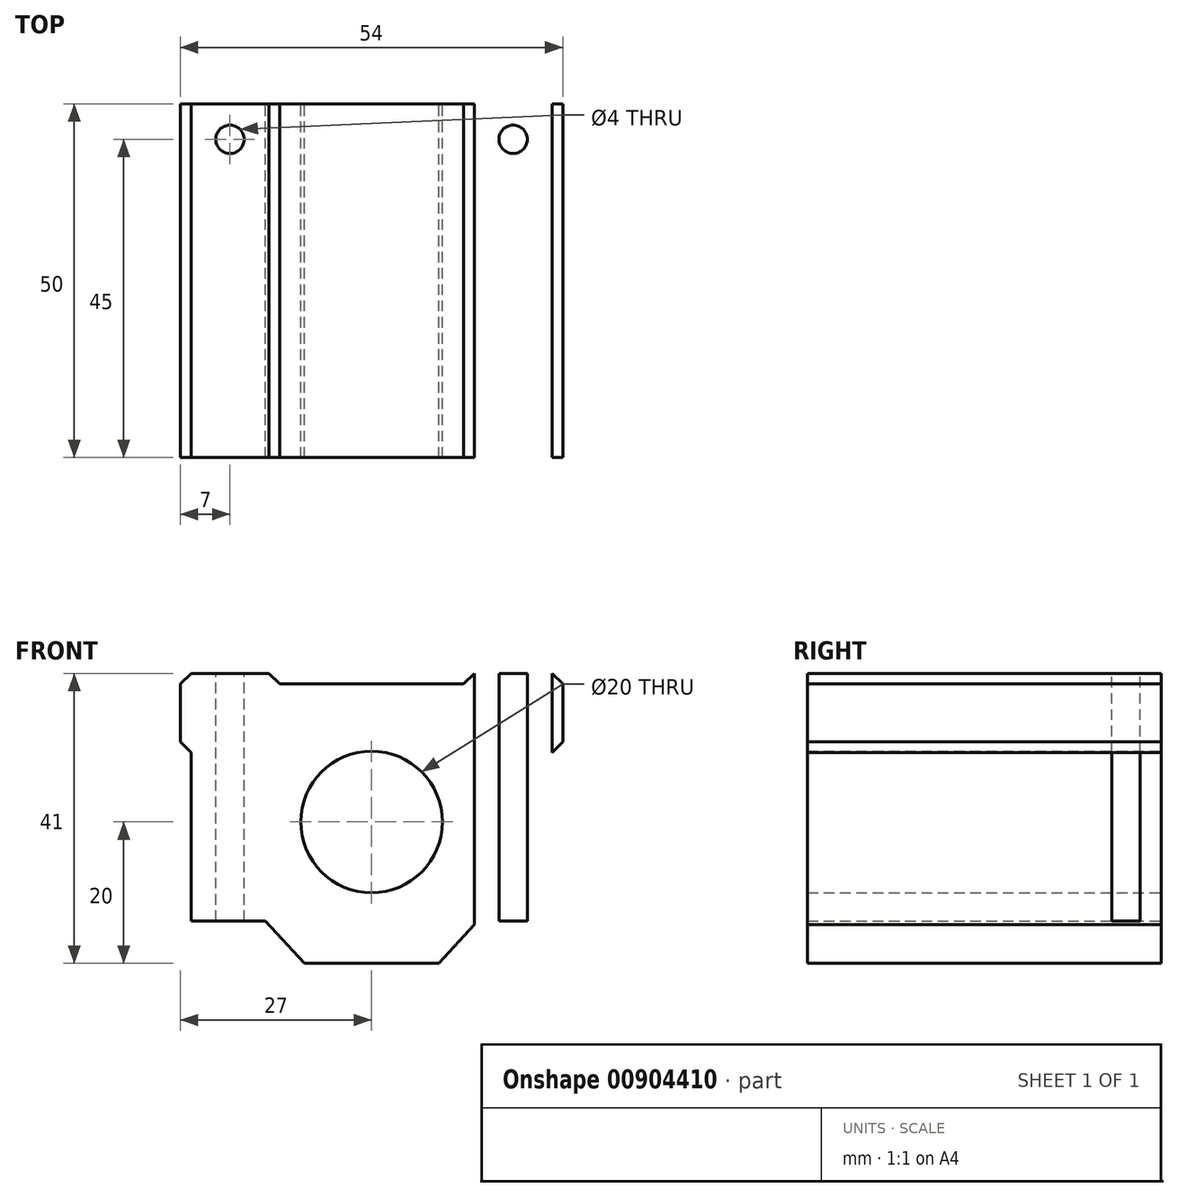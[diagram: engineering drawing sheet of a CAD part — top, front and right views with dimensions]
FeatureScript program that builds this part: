
annotation { "Feature Type Name" : "Feature", "Feature Type Description" : "" }
export const myFeature = defineFeature(function(context is Context, id is Id, definition is map)
    precondition{}
    {
        {
            var Q0;
            Q0=qCreatedBy(makeId("Front.planeOp"),FACE);
            var sketch = newSketch(context, id + "F0", { "sketchPlane" : qUnion([Q0])});
            skLineSegment(sketch, "E0", {"start": v(-9.5, -20) * mm, "end": v(-15, -14) * mm});
            skLineSegment(sketch, "E1", {"start": v(-15, -14) * mm, "end": v(-25.5, -14) * mm});
            skLineSegment(sketch, "E2", {"start": v(-25.5, -14) * mm, "end": v(-25.5, 9.82) * mm});
            skLineSegment(sketch, "E3", {"start": v(-25.5, 9.82) * mm, "end": v(-27, 11.32) * mm});
            skLineSegment(sketch, "E4", {"start": v(-27, 11.32) * mm, "end": v(-27, 19.5) * mm});
            skLineSegment(sketch, "E5", {"start": v(-27, 19.5) * mm, "end": v(-25.5, 21) * mm});
            skLineSegment(sketch, "E6", {"start": v(-25.5, 21) * mm, "end": v(-14.5, 21) * mm});
            skLineSegment(sketch, "E7", {"start": v(-14.5, 21) * mm, "end": v(-13, 19.5) * mm});
            skLineSegment(sketch, "E8.MirrorCS", {"start": v(25.5, 9.82) * mm, "end": v(27, 11.32) * mm});
            skLineSegment(sketch, "E9.MirrorCS", {"start": v(27, 19.5) * mm, "end": v(25.5, 21) * mm});
            skLineSegment(sketch, "E10.MirrorCS", {"start": v(14.5, 21) * mm, "end": v(13, 19.5) * mm});
            skLineSegment(sketch, "E11.MirrorCS", {"start": v(9.5, -20) * mm, "end": v(15, -14) * mm});
            skLineSegment(sketch, "E12.MirrorCS", {"start": v(25.5, -14) * mm, "end": v(25.5, 9.82) * mm});
            skLineSegment(sketch, "E13.MirrorCS", {"start": v(15, -14) * mm, "end": v(25.5, -14) * mm});
            skLineSegment(sketch, "E14.MirrorCS", {"start": v(27, 11.32) * mm, "end": v(27, 19.5) * mm});
            skLineSegment(sketch, "E15.MirrorCS", {"start": v(25.5, 21) * mm, "end": v(14.5, 21) * mm});
            skLineSegment(sketch, "E16", {"start": v(-13, 19.5) * mm, "end": v(13, 19.5) * mm});
            skLineSegment(sketch, "E17", {"start": v(-9.5, -20) * mm, "end": v(9.5, -20) * mm});
            skCircle(sketch, "E18", {"center": v(0, 0) * mm, "radius": 10 * mm});
            skSolve(sketch);
        }
        {
            var Q0;
            Q0=makeQuery(id+"F0.imprint","IMPRINT",FACE,{"disambiguationData":[TD([[makeQuery(id+"F0.imprint","IMPRINT",EDGE,{"derivedFrom":sQuery(id+"F0.wireOp",EDGE,"E0")}),-1.0]])]});
            extrude(context, id + "F1", {"entities" : qUnion([Q0]), "endBound" : BoundingType.SYMMETRIC, "depth" : 50 * mm, "offsetDistance" : 25 * mm});
        }
        {
            var Q0;
            Q0=makeQuery(id+"F1.opExtrude","SWEPT_FACE",FACE,{"disambiguationData":[OSD([sQuery(id+"F0.wireOp",EDGE,"E15.MirrorCS")])]});
            var sketch = newSketch(context, id + "F2", { "sketchPlane" : qUnion([Q0])});
            skLineSegment(sketch, "E19", {"start": v(28.5, 0) * mm, "end": v(-29.66, 0) * mm, "construction": true});
            skLineSegment(sketch, "E20.0", {"start": v(28.5, 20) * mm, "end": v(-29.66, 20) * mm, "construction": true});
            skLineSegment(sketch, "E21.0", {"start": v(28.5, -20) * mm, "end": v(-29.66, -20) * mm, "construction": true});
            skLineSegment(sketch, "E22", {"start": v(0, 26.59) * mm, "end": v(0, -26.5) * mm, "construction": true});
            skLineSegment(sketch, "E23.0", {"start": v(20, 26.59) * mm, "end": v(20, -26.5) * mm, "construction": true});
            skLineSegment(sketch, "E24.0", {"start": v(-20, 26.59) * mm, "end": v(-20, -26.5) * mm, "construction": true});
            skCircle(sketch, "E25", {"center": v(-20, 20) * mm, "radius": 2 * mm});
            skCircle(sketch, "E26.MirrorC", {"center": v(20, 20) * mm, "radius": 2 * mm});
            skCircle(sketch, "E27.MirrorC", {"center": v(-20, -20) * mm, "radius": 2 * mm});
            skCircle(sketch, "E28.MirrorC", {"center": v(20, -20) * mm, "radius": 2 * mm});
            skSolve(sketch);
        }
        {
            var Q0;
            Q0=makeQuery(id+"F2.imprint","IMPRINT",FACE,{"disambiguationData":[TD([[makeQuery(id+"F2.imprint","IMPRINT",EDGE,{"derivedFrom":sQuery(id+"F2.wireOp",EDGE,"E25")}),1.0]])]});
            var Q1;
            Q1=makeQuery(id+"F2.imprint","IMPRINT",FACE,{"disambiguationData":[TD([[makeQuery(id+"F2.imprint","IMPRINT",EDGE,{"derivedFrom":sQuery(id+"F2.wireOp",EDGE,"E26.MirrorC")}),-1.0]])]});
            var Q2;
            Q2=makeQuery(id+"F2.imprint","IMPRINT",FACE,{"disambiguationData":[TD([[makeQuery(id+"F2.imprint","IMPRINT",EDGE,{"derivedFrom":sQuery(id+"F2.wireOp",EDGE,"E28.MirrorC")}),1.0]])]});
            var Q3;
            Q3=makeQuery(id+"F2.imprint","IMPRINT",FACE,{"disambiguationData":[TD([[makeQuery(id+"F2.imprint","IMPRINT",EDGE,{"derivedFrom":sQuery(id+"F2.wireOp",EDGE,"E27.MirrorC")}),-1.0]])]});
            extrude(context, id + "F3", {"entities" : qUnion([Q0, Q1, Q2, Q3]), "operationType" : NewBodyOperationType.REMOVE, "oppositeDirection" : true, "depth" : 40 * mm, "offsetDistance" : 25 * mm});
        }
    });
